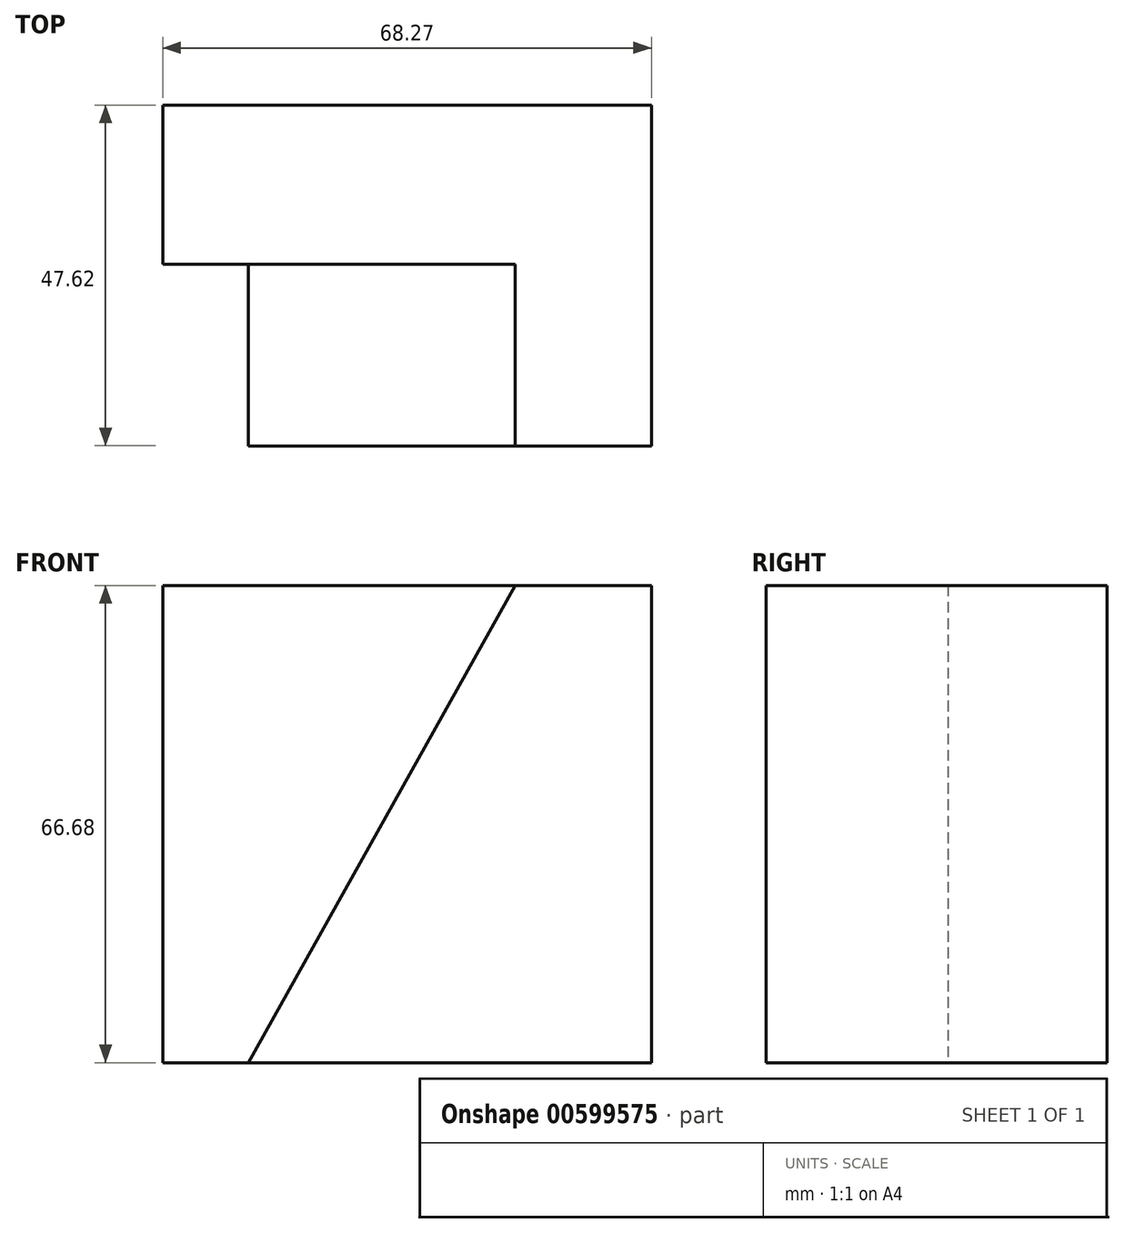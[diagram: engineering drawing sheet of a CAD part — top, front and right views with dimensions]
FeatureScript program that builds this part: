
annotation { "Feature Type Name" : "Feature", "Feature Type Description" : "" }
export const myFeature = defineFeature(function(context is Context, id is Id, definition is map)
    precondition{}
    {
        {
            var Q0;
            Q0=qCreatedBy(makeId("Front.planeOp"),FACE);
            var sketch = newSketch(context, id + "F0", { "sketchPlane" : qUnion([Q0])});
            skLineSegment(sketch, "E0", {"start": v(0, 0) * mm, "end": v(136.52, 0) * mm});
            skLineSegment(sketch, "E1", {"start": v(136.53, 0) * mm, "end": v(136.53, 66.67) * mm});
            skLineSegment(sketch, "E2", {"start": v(136.53, 66.68) * mm, "end": v(0, 66.67) * mm});
            skLineSegment(sketch, "E3", {"start": v(0, 66.67) * mm, "end": v(0, 0) * mm});
            skSolve(sketch);
        }
        {
            var Q0;
            Q0 = qSketchRegion(id + "F0", true);
            extrude(context, id + "F1", {"entities" : qUnion([Q0]), "depth" : 47.62 * mm, "offsetDistance" : 25.4 * mm});
        }
        {
            var Q0;
            Q0=makeQuery(id+"F1.opExtrude","CAP_FACE",FACE,{"disambiguationData":[OSD([sQuery(id+"F0.wireOp",EDGE,"E0"),sQuery(id+"F0.wireOp",EDGE,"E1"),sQuery(id+"F0.wireOp",EDGE,"E2"),sQuery(id+"F0.wireOp",EDGE,"E3")])],"isStart":false});
            var sketch = newSketch(context, id + "F2", { "sketchPlane" : qUnion([Q0])});
            skLineSegment(sketch, "E4", {"start": v(19.05, 66.68) * mm, "end": v(56.32, 0) * mm});
            skLineSegment(sketch, "E5", {"start": v(19.05, 66.68) * mm, "end": v(117.48, 66.68) * mm});
            skLineSegment(sketch, "E6", {"start": v(117.48, 66.68) * mm, "end": v(80.2, 0) * mm});
            skPoint(sketch, "E7.start.orphan", {"position": v(68.26, 0) * mm});
            skLineSegment(sketch, "E8", {"start": v(56.32, 0) * mm, "end": v(80.2, 0) * mm});
            skSolve(sketch);
        }
        {
            var Q0;
            Q0 = qSketchRegion(id + "F2", true);
            extrude(context, id + "F3", {"entities" : qUnion([Q0]), "operationType" : NewBodyOperationType.REMOVE, "oppositeDirection" : true, "depth" : 25.4 * mm, "offsetDistance" : 25.4 * mm});
        }
        {
            var Q0;
            Q0=makeQuery(id+"F1.opExtrude","SWEPT_FACE",FACE,{"disambiguationData":[OSD([sQuery(id+"F0.wireOp",EDGE,"E3")])]});
            extrude(context, id + "F4", {"entities" : qUnion([Q0]), "operationType" : NewBodyOperationType.REMOVE, "oppositeDirection" : true, "depth" : 68.26 * mm, "offsetDistance" : 25.4 * mm});
        }
    });
